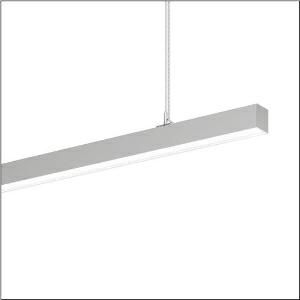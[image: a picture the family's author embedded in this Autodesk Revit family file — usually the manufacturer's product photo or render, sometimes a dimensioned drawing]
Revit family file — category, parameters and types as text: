
# Revit family: silica_r__21_51mx30db35sb_46d1
name_source: partatom
category: Lighting Fixtures
units: mm (PartAtom-declared; Revit-internal decimal feet)

## family parameters
Cut with Voids When Loaded = No
Host = Face
Light Source = No
Part Type = Normal
Room Calculation Point = No
Round Connector Dimension = Use Diameter
Shared = No

## types (1)
- --- (1 x LED, 5260 lm, 34.1 W, 3000K)
    Apparent Load = 34 VA
    CIE Flux Codes = 47 79 96 57 100
    Color Rendering = 80
    Color Temperature = 3000K
    Default Elevation = 1800 mm
    Description = Silica® 21, office luminaire, primary optical cover: cover, of PMMA, opal, light emission: direct/indirect distribution, primary light characteristic: symmetric, installation type: suspended mounting, LED, rated luminous flux: 5.260lm, luminous efficacy: 154lm/W, light colour: 830, colour temperature: 3000K, with terminal, 3+2-pole, max. 2.5mm², mains connection: 220..240V, AC, 50/60Hz, rated input power: 34.1W, luminaire housing, of aluminium, metallic grey (RAL 9006), length: 1.504mm, width: 53mm, height: 53mm, protection rating (complete): IP20, insulation class (complete): insulation class I (protective earthing), certification: CE, permissible operating ambient temperature: 0..+35°C, standard: EN 50419, packaging unit: 1 piece
    Height = 53 mm
    Lamp = 1 x LED
    Lamp Light Flux = 5260 lm
    Lamp Power = 34.1 W
    Lamp count = 1
    Length = 1504 mm
    Luminous efficacy = 154 lm/W
    Manufacturer = Siteco
    ModVariant = No
    Model = 51MX30DB35SB
    Mounting Place = Ceiling
    Mounting Type = Pendant
    Number of Poles = 1
    OnlyDefault = Yes
    Power Factor = 1
    Product Name = Silica® 21
    Product group = office luminaire | ceiling pendant
    ProductGroupID = 902
    Protection Class = Protection class I
    Protection Degree = IP 20
    RLX_Detail_Level = 1
    RLX_Emergency_Light_Flux = 0 lm
    RLX_Emergency_Type = 0
    RLX_Emergency_Type_DB = No
    RlxData = <blob elided: 23421 chars, md5=b18d6b69>
    Socket = socket
    Standby Power = 0 W
    System Light Flux = 5260 lm
    System Power = 34 W
    Type Comments = factory setting: luminous flux: 100 % | dim-lin: 254 | 233 mA
    Type Image = l_1335864.jpg
    URL = http://relux.com
    VarID = @adj_085741
    Voltage = 0 V
    Weight = 0.00 kg
    Width = 53 mm

## geometry (parser evidence)
native form markers: Blend x4, Sweep x12
no freeform markers — native parametric forms only
